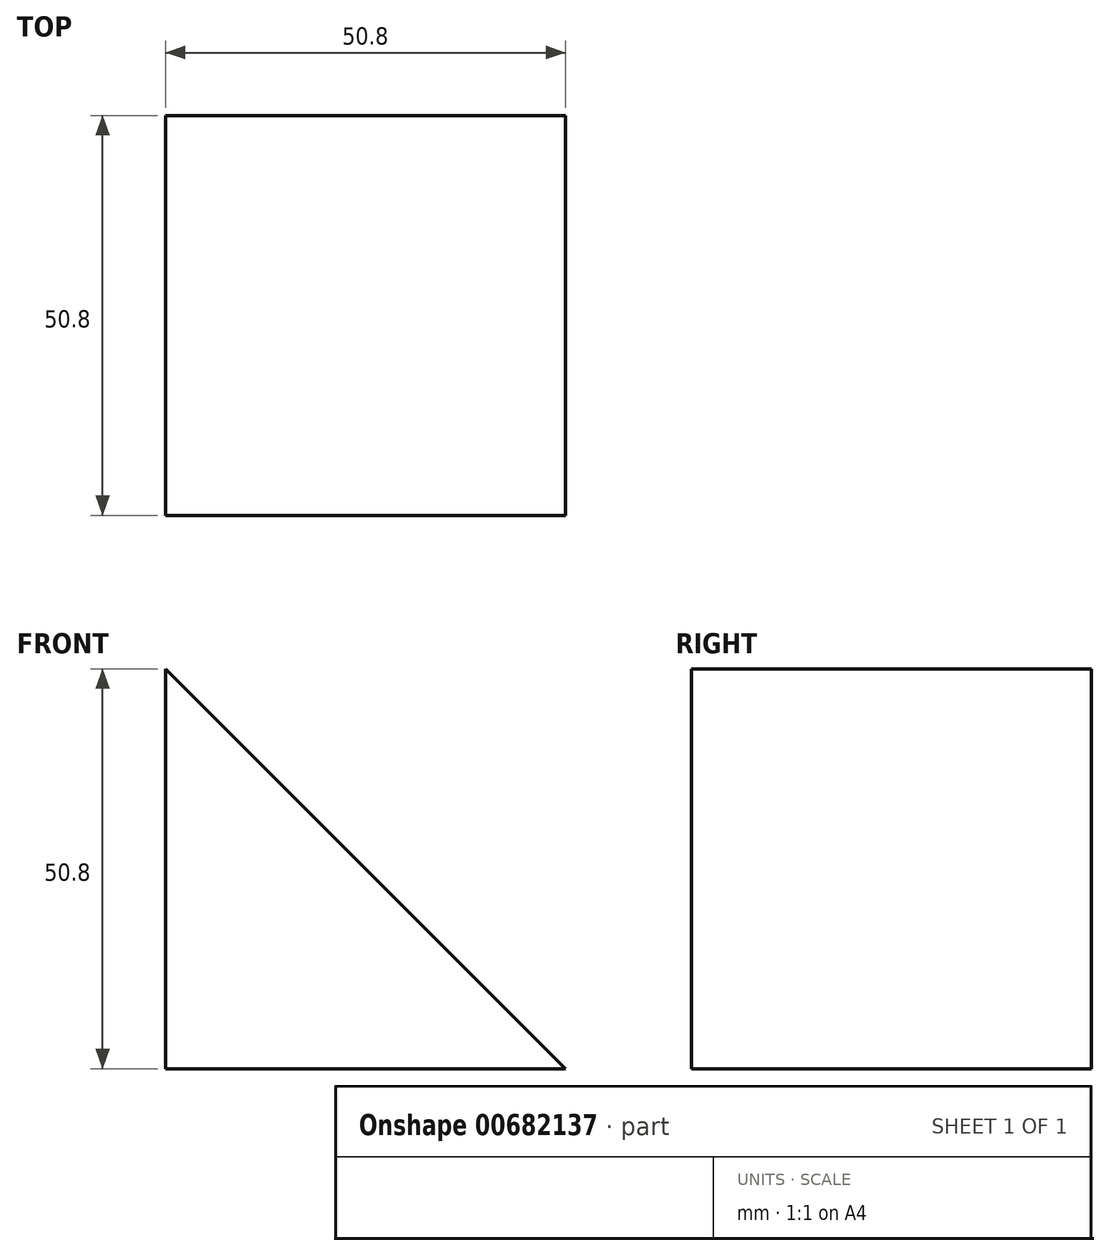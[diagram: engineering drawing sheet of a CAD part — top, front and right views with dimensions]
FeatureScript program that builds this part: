
annotation { "Feature Type Name" : "Feature", "Feature Type Description" : "" }
export const myFeature = defineFeature(function(context is Context, id is Id, definition is map)
    precondition{}
    {
        {
            var Q0;
            Q0=qCreatedBy(makeId("Front.planeOp"),FACE);
            var sketch = newSketch(context, id + "F0", { "sketchPlane" : qUnion([Q0])});
            skLineSegment(sketch, "E0", {"start": v(-34.42, 50.8) * mm, "end": v(-34.42, 0) * mm});
            skLineSegment(sketch, "E1", {"start": v(-34.42, 0) * mm, "end": v(16.38, 0) * mm});
            skLineSegment(sketch, "E2", {"start": v(16.38, 0) * mm, "end": v(-34.42, 50.8) * mm});
            skSolve(sketch);
        }
        {
            var Q0;
            Q0=makeQuery(id+"F0.imprint","IMPRINT",FACE,{"disambiguationData":[TD([[makeQuery(id+"F0.imprint","IMPRINT",EDGE,{"derivedFrom":sQuery(id+"F0.wireOp",EDGE,"E0")}),1.0]])]});
            extrude(context, id + "F1", {"entities" : qUnion([Q0]), "depth" : 50.8 * mm, "offsetDistance" : 25.4 * mm});
        }
    });
